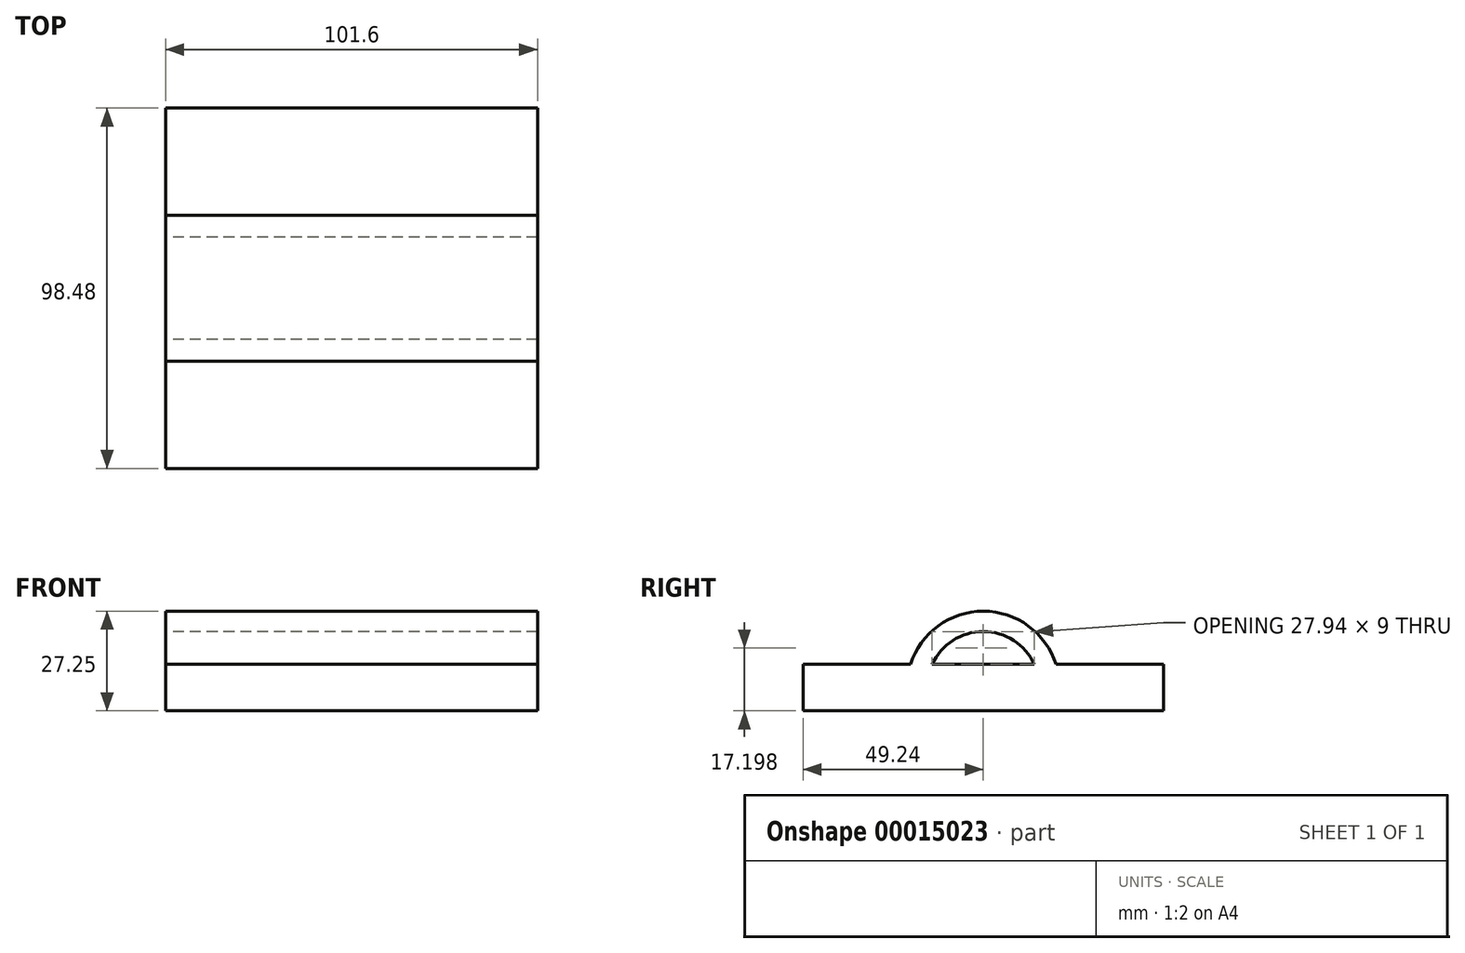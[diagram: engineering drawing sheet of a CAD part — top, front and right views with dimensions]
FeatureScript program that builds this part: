
annotation { "Feature Type Name" : "Feature", "Feature Type Description" : "" }
export const myFeature = defineFeature(function(context is Context, id is Id, definition is map)
    precondition{}
    {
        {
            var Q0;
            Q0=qCreatedBy(makeId("Right.planeOp"),FACE);
            var sketch = newSketch(context, id + "F0", { "sketchPlane" : qUnion([Q0])});
            skLineSegment(sketch, "E0.rect.bottom", {"start": v(-49.24, 6.35) * mm, "end": v(49.24, 6.35) * mm});
            skLineSegment(sketch, "E0.rect.top", {"start": v(-49.24, -6.35) * mm, "end": v(49.24, -6.35) * mm});
            skLineSegment(sketch, "E0.rect.left", {"start": v(-49.24, 6.35) * mm, "end": v(-49.24, -6.35) * mm});
            skLineSegment(sketch, "E0.rect.right", {"start": v(49.24, 6.35) * mm, "end": v(49.24, -6.35) * mm});
            skPoint(sketch, "E0.rect.middle", {"position": v(0, 0) * mm});
            skArc(sketch, "E1", {"start": v(13.97, 6.35) * mm, "mid": v(0, 15.35) * mm, "end": v(-13.97, 6.35) * mm});
            skArc(sketch, "E2", {"start": v(19.9, -6.35) * mm, "mid": v(0, 20.9) * mm, "end": v(-19.9, -6.35) * mm});
            skSolve(sketch);
        }
        {
            var Q0;
            {var subQ5=sQuery(id+"F0.wireOp",EDGE,"E0.rect.left");Q0=makeQuery(id+"F0.imprint","IMPRINT",FACE,{"disambiguationData":[TD([[makeQuery(id+"F0.imprint","IMPRINT",EDGE,{"derivedFrom":subQ5}),1.0]])]});}
            var Q1;
            {var subQ0=sQuery(id+"F0.wireOp",EDGE,"E1");Q1=makeQuery(id+"F0.imprint","IMPRINT",FACE,{"disambiguationData":[TD([[makeQuery(id+"F0.imprint","IMPRINT",EDGE,{"derivedFrom":subQ0}),-1.0]])]});}
            var Q2;
            {var subQ1=sQuery(id+"F0.wireOp",EDGE,"E0.rect.bottom");var subQ7=sQuery(id+"F0.wireOp",EDGE,"E1");var subQ9=makeQuery(id+"F0.imprint","INTERSECT",VERTEX,{"disambiguationData":[OD(1.0)],"derivedFrom":[subQ1,subQ7]});Q2=makeQuery(id+"F0.imprint","IMPRINT",FACE,{"disambiguationData":[TD([[makeQuery(id+"F0.imprint","IMPRINT",EDGE,{"disambiguationData":[TD([[subQ9,1.0]])],"derivedFrom":subQ1}),-1.0]])]});}
            var Q3;
            {var subQ5=sQuery(id+"F0.wireOp",EDGE,"E0.rect.right");Q3=makeQuery(id+"F0.imprint","IMPRINT",FACE,{"disambiguationData":[TD([[makeQuery(id+"F0.imprint","IMPRINT",EDGE,{"derivedFrom":subQ5}),-1.0]])]});}
            extrude(context, id + "F1", {"entities" : qUnion([Q0, Q1, Q2, Q3]), "endBound" : BoundingType.SYMMETRIC, "depth" : 101.6 * mm});
        }
    });
